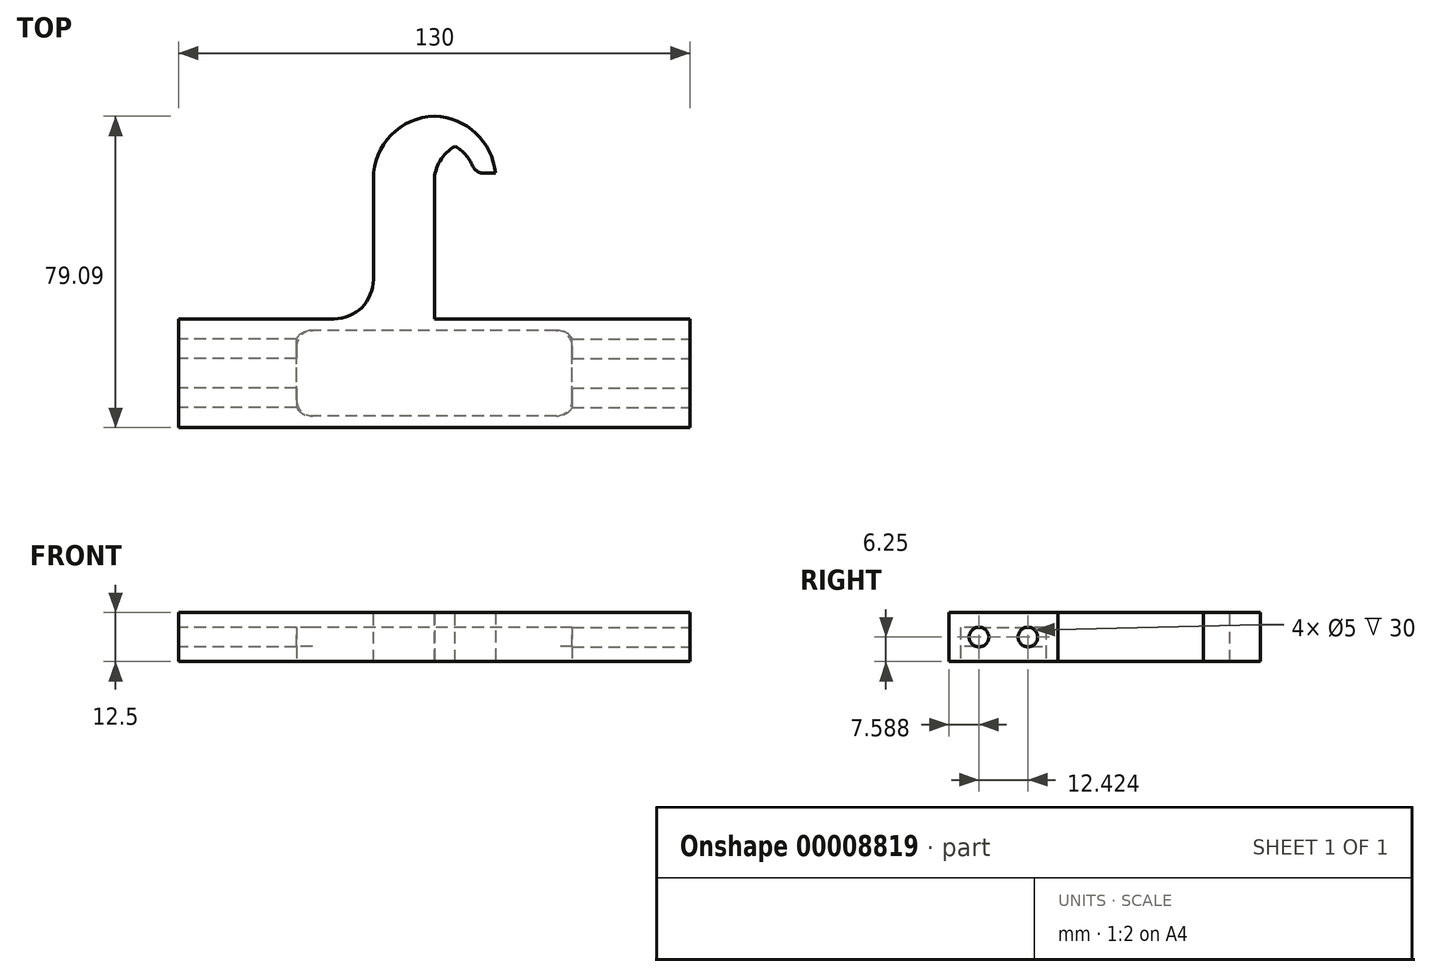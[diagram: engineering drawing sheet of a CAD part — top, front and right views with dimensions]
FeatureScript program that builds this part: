
annotation { "Feature Type Name" : "Feature", "Feature Type Description" : "" }
export const myFeature = defineFeature(function(context is Context, id is Id, definition is map)
    precondition{}
    {
        {
            var Q0;
            Q0=qCreatedBy(makeId("Top.planeOp"),FACE);
            var sketch = newSketch(context, id + "F0", { "sketchPlane" : qUnion([Q0])});
            skLineSegment(sketch, "E0.rect.bottom", {"start": v(32.5, -13.8) * mm, "end": v(-32.5, -13.8) * mm});
            skLineSegment(sketch, "E0.rect.top", {"start": v(32.5, 13.8) * mm, "end": v(-32.5, 13.8) * mm});
            skLineSegment(sketch, "E0.rect.left", {"start": v(32.5, -13.8) * mm, "end": v(32.5, 13.8) * mm});
            skLineSegment(sketch, "E0.rect.right", {"start": v(-32.5, -13.8) * mm, "end": v(-32.5, 13.8) * mm});
            skPoint(sketch, "E0.rect.middle", {"position": v(0, 0) * mm});
            skSolve(sketch);
        }
        {
            var Q0;
            Q0 = qSketchRegion(id + "F0", true);
            extrude(context, id + "F1", {"entities" : qUnion([Q0]), "depth" : 12.5 * mm});
        }
        {
            var Q0;
            Q0=makeQuery(id+"F1.opExtrude","SWEPT_FACE",FACE,{"disambiguationData":[OSD([sQuery(id+"F0.wireOp",EDGE,"E0.rect.right")])]});
            var sketch = newSketch(context, id + "F2", { "sketchPlane" : qUnion([Q0])});
            skLineSegment(sketch, "E1", {"start": v(0, 12.5) * mm, "end": v(0, 0) * mm});
            skLineSegment(sketch, "E2.rect.bottom", {"start": v(-3.71, 0) * mm, "end": v(-8.71, 0) * mm});
            skLineSegment(sketch, "E2.rect.top", {"start": v(-3.71, 8.75) * mm, "end": v(-8.71, 8.75) * mm});
            skLineSegment(sketch, "E2.rect.left", {"start": v(-3.71, 0) * mm, "end": v(-3.71, 8.75) * mm});
            skLineSegment(sketch, "E2.rect.right", {"start": v(-8.71, 0) * mm, "end": v(-8.71, 8.75) * mm});
            skPoint(sketch, "E2.rect.middle", {"position": v(-6.21, 4.38) * mm});
            skLineSegment(sketch, "E3.rect.bottom", {"start": v(8.71, 0) * mm, "end": v(3.71, 0) * mm});
            skLineSegment(sketch, "E3.rect.top", {"start": v(8.71, 8.75) * mm, "end": v(3.71, 8.75) * mm});
            skLineSegment(sketch, "E3.rect.left", {"start": v(8.71, 0) * mm, "end": v(8.71, 8.75) * mm});
            skLineSegment(sketch, "E3.rect.right", {"start": v(3.71, 0) * mm, "end": v(3.71, 8.75) * mm});
            skPoint(sketch, "E3.rect.middle", {"position": v(6.21, 4.38) * mm});
            skLineSegment(sketch, "E4", {"start": v(0, 6.25) * mm, "end": v(6.21, 6.25) * mm});
            skLineSegment(sketch, "E5", {"start": v(0, 6.25) * mm, "end": v(-6.21, 6.25) * mm});
            skCircle(sketch, "E6", {"center": v(-6.21, 6.25) * mm, "radius": 2.5 * mm});
            skCircle(sketch, "E7", {"center": v(6.21, 6.25) * mm, "radius": 2.5 * mm});
            skSolve(sketch);
        }
        {
            var Q0;
            {var subQ0=sQuery(id+"F2.wireOp",EDGE,"E6");var subQ3=makeQuery(id+"F2.imprint","INTERSECT",VERTEX,{"derivedFrom":[sQuery(id+"F2.wireOp",EDGE,"E2.rect.top"),subQ0]});Q0=makeQuery(id+"F2.imprint","IMPRINT",FACE,{"disambiguationData":[TD([[makeQuery(id+"F2.imprint","IMPRINT",EDGE,{"disambiguationData":[TD([[subQ3,-1.0]])],"derivedFrom":subQ0}),1.0]])]});}
            var Q1;
            {var subQ0=sQuery(id+"F2.wireOp",EDGE,"E7");var subQ3=makeQuery(id+"F2.imprint","INTERSECT",VERTEX,{"derivedFrom":[sQuery(id+"F2.wireOp",EDGE,"E3.rect.top"),subQ0]});Q1=makeQuery(id+"F2.imprint","IMPRINT",FACE,{"disambiguationData":[TD([[makeQuery(id+"F2.imprint","IMPRINT",EDGE,{"disambiguationData":[TD([[subQ3,1.0]])],"derivedFrom":subQ0}),1.0]])]});}
            extrude(context, id + "F3", {"entities" : qUnion([Q0, Q1]), "operationType" : NewBodyOperationType.REMOVE, "oppositeDirection" : true, "depth" : 30 * mm});
        }
        {
            var Q0;
            Q0=makeQuery(id+"F1.opExtrude","CAP_FACE",FACE,{"disambiguationData":[OSD([sQuery(id+"F0.wireOp",EDGE,"E0.rect.bottom"),sQuery(id+"F0.wireOp",EDGE,"E0.rect.top"),sQuery(id+"F0.wireOp",EDGE,"E0.rect.left"),sQuery(id+"F0.wireOp",EDGE,"E0.rect.right")])],"isStart":true});
            var sketch = newSketch(context, id + "F4", { "sketchPlane" : qUnion([Q0])});
            skLineSegment(sketch, "E8.rect.bottom", {"start": v(-2.5, 10.86) * mm, "end": v(67.5, 10.86) * mm});
            skLineSegment(sketch, "E8.rect.top", {"start": v(-2.5, -10.86) * mm, "end": v(67.5, -10.86) * mm});
            skLineSegment(sketch, "E8.rect.left", {"start": v(-2.5, 10.86) * mm, "end": v(-2.5, -10.86) * mm});
            skLineSegment(sketch, "E8.rect.right", {"start": v(67.5, 10.86) * mm, "end": v(67.5, -10.86) * mm});
            skPoint(sketch, "E8.rect.middle", {"position": v(32.5, 0) * mm});
            skSolve(sketch);
        }
        {
            var Q0;
            {var subQ3=sQuery(id+"F4.wireOp",EDGE,"E8.rect.bottom");var subQ5=sQuery(id+"F4.wireOp",EDGE,"E8.rect.left");var subQ14=makeQuery(id+"F4.imprint","INTERSECT",VERTEX,{"derivedFrom":[subQ3,subQ5]});Q0=makeQuery(id+"F4.imprint","IMPRINT",FACE,{"disambiguationData":[TD([[makeQuery(id+"F4.imprint","IMPRINT",EDGE,{"disambiguationData":[TD([[subQ14,-1.0]])],"derivedFrom":subQ3}),-1.0]])]});}
            extrude(context, id + "F5", {"entities" : qUnion([Q0]), "operationType" : NewBodyOperationType.REMOVE, "oppositeDirection" : true, "depth" : 8.75 * mm});
        }
        {
            var Q0;
            Q0=makeQuery(id+"F1.opExtrude","SWEPT_BODY",BODY,{"disambiguationData":[OSD([sQuery(id+"F0.wireOp",EDGE,"E0.rect.bottom"),sQuery(id+"F0.wireOp",EDGE,"E0.rect.top"),sQuery(id+"F0.wireOp",EDGE,"E0.rect.left"),sQuery(id+"F0.wireOp",EDGE,"E0.rect.right")])]});
            var Q1;
            Q1=makeQuery(id+"F1.opExtrude","SWEPT_FACE",FACE,{"disambiguationData":[OSD([sQuery(id+"F0.wireOp",EDGE,"E0.rect.left")])]});
            mirror(context, id + "F6", {"entities" : qUnion([Q0]), "mirrorPlane" : qUnion([Q1])});
        }
        {
            var Q0;
            Q0=makeQuery(id+"F6.opPattern","COPY",BODY,{"derivedFrom":makeQuery(id+"F1.opExtrude","SWEPT_BODY",BODY,{"disambiguationData":[OSD([sQuery(id+"F0.wireOp",EDGE,"E0.rect.bottom"),sQuery(id+"F0.wireOp",EDGE,"E0.rect.top"),sQuery(id+"F0.wireOp",EDGE,"E0.rect.left"),sQuery(id+"F0.wireOp",EDGE,"E0.rect.right")])]}),"instanceName":"1"});
            var Q1;
            Q1=makeQuery(id+"F1.opExtrude","SWEPT_BODY",BODY,{"disambiguationData":[OSD([sQuery(id+"F0.wireOp",EDGE,"E0.rect.bottom"),sQuery(id+"F0.wireOp",EDGE,"E0.rect.top"),sQuery(id+"F0.wireOp",EDGE,"E0.rect.left"),sQuery(id+"F0.wireOp",EDGE,"E0.rect.right")])]});
            booleanBodies(context, id + "F7", {"operationType" : BooleanOperationType.UNION, "tools" : qUnion([Q0, Q1])});
        }
        {
            var Q0;
            {var subQ0=makeQuery(id+"F1.opExtrude","SWEPT_FACE",FACE,{"disambiguationData":[OSD([sQuery(id+"F0.wireOp",EDGE,"E0.rect.top")])]});Q0=makeQuery(id+"F7.opBoolean","MERGE",FACE,{"derivedFrom":[subQ0,makeQuery(id+"F6.opPattern","COPY",FACE,{"derivedFrom":subQ0,"instanceName":"1"})]});}
            var sketch = newSketch(context, id + "F8", { "sketchPlane" : qUnion([Q0])});
            skLineSegment(sketch, "E9", {"start": v(-32.5, 12.5) * mm, "end": v(-32.5, 0) * mm});
            skLineSegment(sketch, "E10.rect.bottom", {"start": v(-23, 0) * mm, "end": v(-42, 0) * mm});
            skLineSegment(sketch, "E10.rect.top", {"start": v(-23, 12.5) * mm, "end": v(-42, 12.5) * mm});
            skLineSegment(sketch, "E10.rect.left", {"start": v(-23, 0) * mm, "end": v(-23, 12.5) * mm});
            skLineSegment(sketch, "E10.rect.right", {"start": v(-42, 0) * mm, "end": v(-42, 12.5) * mm});
            skPoint(sketch, "E10.rect.middle", {"position": v(-32.5, 6.25) * mm});
            skLineSegment(sketch, "E11.rect.bottom", {"start": v(-17, 0) * mm, "end": v(-48, 0) * mm});
            skLineSegment(sketch, "E11.rect.top", {"start": v(-17, 12.5) * mm, "end": v(-48, 12.5) * mm});
            skLineSegment(sketch, "E11.rect.left", {"start": v(-17, 0) * mm, "end": v(-17, 12.5) * mm});
            skLineSegment(sketch, "E11.rect.right", {"start": v(-48, 0) * mm, "end": v(-48, 12.5) * mm});
            skSolve(sketch);
        }
        {
            var Q0;
            {var subQ4=sQuery(id+"F8.wireOp",EDGE,"E10.rect.left");Q0=makeQuery(id+"F8.imprint","IMPRINT",FACE,{"disambiguationData":[TD([[makeQuery(id+"F8.imprint","IMPRINT",EDGE,{"derivedFrom":subQ4}),-1.0]])]});}
            var Q1;
            {var subQ2=sQuery(id+"F8.wireOp",EDGE,"E9");Q1=makeQuery(id+"F8.imprint","IMPRINT",FACE,{"disambiguationData":[TD([[makeQuery(id+"F8.imprint","IMPRINT",EDGE,{"derivedFrom":subQ2}),1.0]])]});}
            var Q2;
            {var subQ2=sQuery(id+"F8.wireOp",EDGE,"E9");Q2=makeQuery(id+"F8.imprint","IMPRINT",FACE,{"disambiguationData":[TD([[makeQuery(id+"F8.imprint","IMPRINT",EDGE,{"derivedFrom":subQ2}),-1.0]])]});}
            var Q3;
            {var subQ4=sQuery(id+"F8.wireOp",EDGE,"E10.rect.right");Q3=makeQuery(id+"F8.imprint","IMPRINT",FACE,{"disambiguationData":[TD([[makeQuery(id+"F8.imprint","IMPRINT",EDGE,{"derivedFrom":subQ4}),1.0]])]});}
            extrude(context, id + "F9", {"entities" : qUnion([Q0, Q1, Q2, Q3]), "operationType" : NewBodyOperationType.ADD, "depth" : 51.5 * mm});
        }
        {
            var Q0;
            {var subQ0=sQuery(id+"F0.wireOp",EDGE,"E0.rect.top");var subQ1=sQuery(id+"F0.wireOp",EDGE,"E0.rect.left");var subQ2=sQuery(id+"F0.wireOp",EDGE,"E0.rect.right");var subQ3=makeQuery(id+"F5.boolean.opBoolean","SPLIT",FACE,{"disambiguationData":[TD([makeQuery(id+"F1.opExtrude","SWEPT_FACE",FACE,{"disambiguationData":[OSD([subQ0])]})])],"derivedFrom":makeQuery(id+"F1.opExtrude","CAP_FACE",FACE,{"disambiguationData":[OSD([sQuery(id+"F0.wireOp",EDGE,"E0.rect.bottom"),subQ0,subQ1,subQ2])],"isStart":true})});Q0=makeQuery(id+"F9.boolean.opBoolean","MERGE",FACE,{"derivedFrom":[makeQuery(id+"F7.opBoolean","MERGE",FACE,{"derivedFrom":[subQ3,makeQuery(id+"F6.opPattern","COPY",FACE,{"derivedFrom":subQ3,"instanceName":"1"})]}),makeQuery(id+"F9.opExtrude","SWEPT_FACE",FACE,{"disambiguationData":[OSD([sQuery(id+"F8.wireOp",EDGE,"E11.rect.bottom")])]})]});}
            var sketch = newSketch(context, id + "F10", { "sketchPlane" : qUnion([Q0])});
            skLineSegment(sketch, "E12", {"start": v(48, -13.8) * mm, "end": v(17, -13.8) * mm});
            skLineSegment(sketch, "E13", {"start": v(17, -13.8) * mm, "end": v(32.5, -13.8) * mm});
            skLineSegment(sketch, "E14.bottom", {"start": v(32.5, -13.8) * mm, "end": v(23, -13.8) * mm});
            skLineSegment(sketch, "E14.top", {"start": v(32.5, -58.8) * mm, "end": v(23, -58.8) * mm});
            skLineSegment(sketch, "E14.left", {"start": v(32.5, -13.8) * mm, "end": v(32.5, -58.8) * mm});
            skLineSegment(sketch, "E14.right", {"start": v(23, -13.8) * mm, "end": v(23, -58.8) * mm});
            skLineSegment(sketch, "E15.bottom", {"start": v(32.5, -13.8) * mm, "end": v(42, -13.8) * mm});
            skLineSegment(sketch, "E15.top", {"start": v(32.5, -58.8) * mm, "end": v(42, -58.8) * mm});
            skLineSegment(sketch, "E15.right", {"start": v(42, -13.8) * mm, "end": v(42, -58.8) * mm});
            skLineSegment(sketch, "E16", {"start": v(32.5, -13.8) * mm, "end": v(32.5, -50.8) * mm});
            skLineSegment(sketch, "E17", {"start": v(32.5, -50.8) * mm, "end": v(48, -50.8) * mm});
            skSolve(sketch);
        }
        {
            var Q0;
            {var subQ12=sQuery(id+"F10.wireOp",EDGE,"E12");Q0=makeQuery(id+"F10.imprint","IMPRINT",FACE,{"disambiguationData":[TD([[makeQuery(id+"F10.imprint","IMPRINT",EDGE,{"derivedFrom":subQ12}),1.0]])]});}
            var Q1;
            {var subQ4=sQuery(id+"F10.wireOp",EDGE,"E15.bottom");Q1=makeQuery(id+"F10.imprint","IMPRINT",FACE,{"disambiguationData":[TD([[makeQuery(id+"F10.imprint","IMPRINT",EDGE,{"derivedFrom":subQ4}),-1.0]])]});}
            var Q2;
            Q2=makeQuery(id+"F10.imprint","IMPRINT",FACE,{"disambiguationData":[TD([[makeQuery(id+"F10.imprint","IMPRINT",EDGE,{"derivedFrom":sQuery(id+"F10.wireOp",EDGE,"E14.bottom")}),1.0]])]});
            var Q3;
            {var subQ4=sQuery(id+"F10.wireOp",EDGE,"E15.top");Q3=makeQuery(id+"F10.imprint","IMPRINT",FACE,{"disambiguationData":[TD([[makeQuery(id+"F10.imprint","IMPRINT",EDGE,{"derivedFrom":subQ4}),1.0]])]});}
            extrude(context, id + "F11", {"entities" : qUnion([Q0, Q1, Q2, Q3]), "operationType" : NewBodyOperationType.REMOVE, "oppositeDirection" : true, "depth" : 25 * mm});
        }
        {
            var Q0;
            Q0=makeQuery(id+"F11.boolean.opBoolean","COPY",EDGE,{"derivedFrom":makeQuery(id+"F11.opExtrude","SWEPT_EDGE",EDGE,{"disambiguationData":[OSD([sQuery(id+"F10.wireOp",EDGE,"E15.right"),sQuery(id+"F10.wireOp",EDGE,"E17")])]})});
            var Q1;
            Q1=makeQuery(id+"F11.boolean.opBoolean","COPY",EDGE,{"derivedFrom":makeQuery(id+"F11.opExtrude","SWEPT_EDGE",EDGE,{"disambiguationData":[OSD([sQuery(id+"F0.wireOp",EDGE,"E0.rect.top"),sQuery(id+"F8.wireOp",EDGE,"E11.rect.bottom"),sQuery(id+"F8.wireOp",EDGE,"E11.rect.right"),sQuery(id+"F10.wireOp",EDGE,"E17")])]})});
            fillet(context, id + "F12", {"entities" : qUnion([Q0, Q1]), "radius" : 3 * mm, "tangentPropagation" : true, "allowEdgeOverflow" : false});
        }
        {
            var Q0;
            Q0=makeQuery(id+"F11.boolean.opBoolean","COPY",EDGE,{"derivedFrom":makeQuery(id+"F11.opExtrude","SWEPT_EDGE",EDGE,{"disambiguationData":[OSD([sQuery(id+"F10.wireOp",EDGE,"E15.top"),sQuery(id+"F10.wireOp",EDGE,"E15.right")])]})});
            var Q1;
            Q1=makeQuery(id+"F11.boolean.opBoolean","COPY",EDGE,{"derivedFrom":makeQuery(id+"F11.opExtrude","SWEPT_EDGE",EDGE,{"disambiguationData":[OSD([sQuery(id+"F10.wireOp",EDGE,"E14.top"),sQuery(id+"F10.wireOp",EDGE,"E14.right")])]})});
            fillet(context, id + "F13", {"entities" : qUnion([Q0, Q1]), "radius" : 10 * mm, "tangentPropagation" : true, "allowEdgeOverflow" : false});
        }
        {
            var Q0;
            Q0=makeQuery(id+"F9.opExtrude","CAP_EDGE",EDGE,{"disambiguationData":[OSD([sQuery(id+"F8.wireOp",EDGE,"E11.rect.right")])],"isStart":false});
            var Q1;
            Q1=makeQuery(id+"F9.opExtrude","CAP_EDGE",EDGE,{"disambiguationData":[OSD([sQuery(id+"F8.wireOp",EDGE,"E11.rect.left")])],"isStart":false});
            fillet(context, id + "F14", {"entities" : qUnion([Q0, Q1]), "radius" : 16 * mm, "tangentPropagation" : true, "allowEdgeOverflow" : false});
        }
        {
            var Q0;
            Q0=makeQuery(id+"F11.boolean.opBoolean","COPY",EDGE,{"derivedFrom":makeQuery(id+"F11.opExtrude","SWEPT_EDGE",EDGE,{"disambiguationData":[OSD([sQuery(id+"F10.wireOp",EDGE,"E13"),sQuery(id+"F10.wireOp",EDGE,"E14.bottom"),sQuery(id+"F10.wireOp",EDGE,"E14.right")])]})});
            var Q1;
            Q1=makeQuery(id+"F9.opExtrude","CAP_EDGE",EDGE,{"disambiguationData":[OSD([sQuery(id+"F8.wireOp",EDGE,"E11.rect.left")])],"isStart":true});
            fillet(context, id + "F15", {"entities" : qUnion([Q0, Q1]), "radius" : 10 * mm, "tangentPropagation" : true, "allowEdgeOverflow" : false});
        }
        {
            var Q0;
            Q0=makeQuery(id+"F6.opPattern","COPY",EDGE,{"derivedFrom":makeQuery(id+"F5.boolean.opBoolean","COPY",EDGE,{"derivedFrom":makeQuery(id+"F5.opExtrude","SWEPT_EDGE",EDGE,{"disambiguationData":[OSD([sQuery(id+"F4.wireOp",EDGE,"E8.rect.top"),sQuery(id+"F4.wireOp",EDGE,"E8.rect.left")])]})}),"instanceName":"1"});
            var Q1;
            Q1=makeQuery(id+"F5.boolean.opBoolean","COPY",EDGE,{"derivedFrom":makeQuery(id+"F5.opExtrude","SWEPT_EDGE",EDGE,{"disambiguationData":[OSD([sQuery(id+"F4.wireOp",EDGE,"E8.rect.top"),sQuery(id+"F4.wireOp",EDGE,"E8.rect.left")])]})});
            var Q2;
            Q2=makeQuery(id+"F5.boolean.opBoolean","COPY",EDGE,{"derivedFrom":makeQuery(id+"F5.opExtrude","SWEPT_EDGE",EDGE,{"disambiguationData":[OSD([sQuery(id+"F4.wireOp",EDGE,"E8.rect.bottom"),sQuery(id+"F4.wireOp",EDGE,"E8.rect.left")])]})});
            var Q3;
            Q3=makeQuery(id+"F6.opPattern","COPY",EDGE,{"derivedFrom":makeQuery(id+"F5.boolean.opBoolean","COPY",EDGE,{"derivedFrom":makeQuery(id+"F5.opExtrude","SWEPT_EDGE",EDGE,{"disambiguationData":[OSD([sQuery(id+"F4.wireOp",EDGE,"E8.rect.bottom"),sQuery(id+"F4.wireOp",EDGE,"E8.rect.left")])]})}),"instanceName":"1"});
            fillet(context, id + "F16", {"entities" : qUnion([Q0, Q1, Q2, Q3]), "radius" : 4 * mm, "tangentPropagation" : true, "allowEdgeOverflow" : false});
        }
    });
